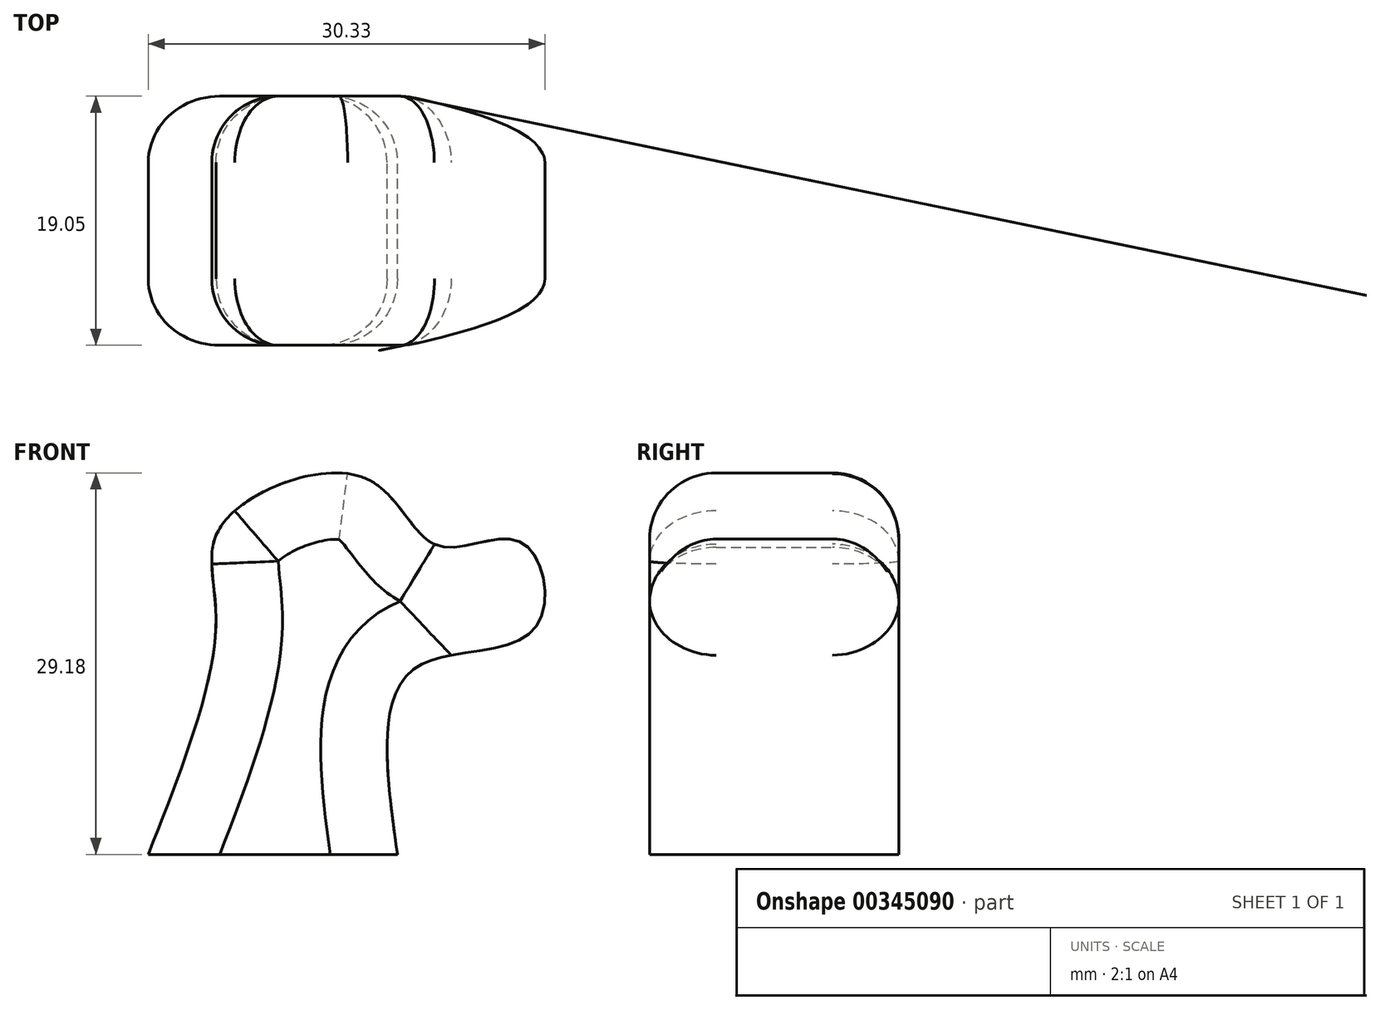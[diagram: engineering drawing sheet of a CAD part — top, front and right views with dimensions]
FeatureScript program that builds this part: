
annotation { "Feature Type Name" : "Feature", "Feature Type Description" : "" }
export const myFeature = defineFeature(function(context is Context, id is Id, definition is map)
    precondition{}
    {
        {
            var Q0;
            Q0=qCreatedBy(makeId("Front.planeOp"),FACE);
            var sketch = newSketch(context, id + "F0", { "sketchPlane" : qUnion([Q0])});
            skLineSegment(sketch, "E0", {"start": v(0, 0) * mm, "end": v(19.05, 0) * mm});
            skFitSpline(sketch, "E1", {"points": [v(0, 0) * mm, v(5.2, 17.94) * mm, v(5.66, 25.25) * mm, v(16.52, 28.8) * mm, v(22.19, 23.6) * mm, v(28.56, 23.84) * mm, v(29.5, 17.23) * mm, v(20.3, 14.16) * mm, v(19.05, 0) * mm], "startDerivative": vector(45.36, 115.14) * mm, "endDerivative": vector(16.77, -120.3) * mm});
            skSolve(sketch);
        }
        {
            var Q0;
            Q0 = qSketchRegion(id + "F0", true);
            extrude(context, id + "F1", {"entities" : qUnion([Q0]), "depth" : 19.05 * mm});
        }
        {
            var Q0;
            Q0=makeQuery(id+"F1.opExtrude","CAP_EDGE",EDGE,{"disambiguationData":[OSD([sQuery(id+"F0.wireOp",EDGE,"E1")])],"isStart":true});
            fillet(context, id + "F2", {"entities" : qUnion([Q0]), "radius" : 5.08 * mm, "tangentPropagation" : true, "allowEdgeOverflow" : false});
        }
        {
            var Q0;
            Q0=makeQuery(id+"F1.opExtrude","CAP_EDGE",EDGE,{"disambiguationData":[OSD([sQuery(id+"F0.wireOp",EDGE,"E1")])],"isStart":false});
            fillet(context, id + "F3", {"entities" : qUnion([Q0]), "radius" : 5.08 * mm, "tangentPropagation" : true, "allowEdgeOverflow" : false});
        }
    });
